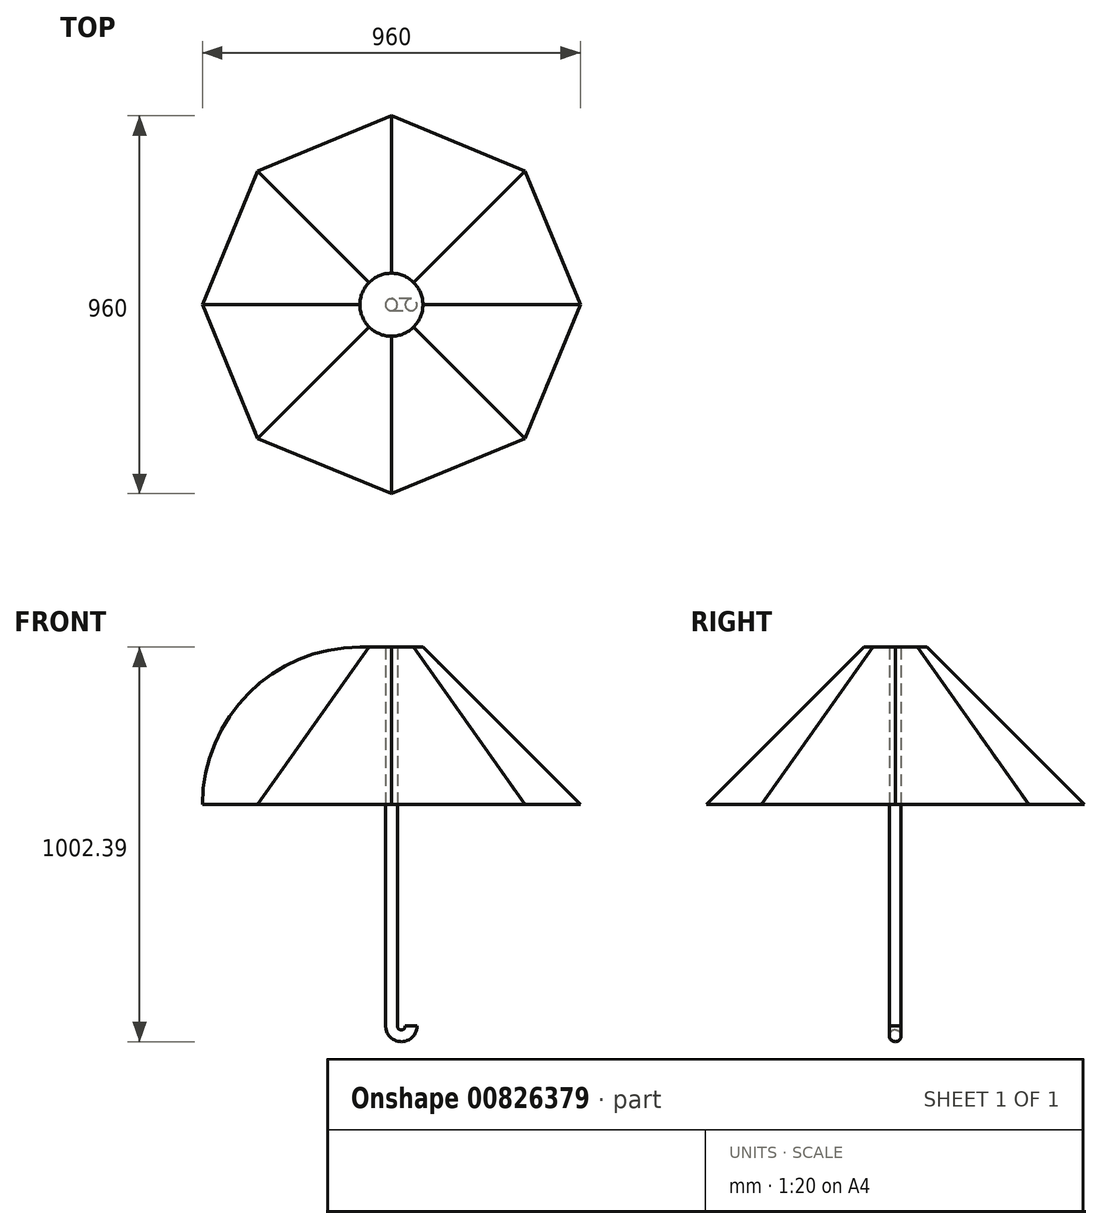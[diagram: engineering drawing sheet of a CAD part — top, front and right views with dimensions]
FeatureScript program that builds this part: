
annotation { "Feature Type Name" : "Feature", "Feature Type Description" : "" }
export const myFeature = defineFeature(function(context is Context, id is Id, definition is map)
    precondition{}
    {
        {
            var Q0;
            Q0=qCreatedBy(makeId("Top.planeOp"),FACE);
            cPlane(context, id + "F0", {"entities" : qUnion([Q0]), "cplaneType" : CPlaneType.OFFSET, "offset" : 400 * mm, "width" : 150 * mm, "height" : 150 * mm});
        }
        {
            var Q0;
            Q0=qCreatedBy(id+"F0.planeOp",FACE);
            var sketch = newSketch(context, id + "F1", { "sketchPlane" : qUnion([Q0])});
            skCircle(sketch, "E0", {"center": v(0, 0) * mm, "radius": 80 * mm});
            skSolve(sketch);
        }
        {
            var Q0;
            Q0=qCreatedBy(makeId("Top.planeOp"),FACE);
            var sketch = newSketch(context, id + "F2", { "sketchPlane" : qUnion([Q0])});
            skCircle(sketch, "E1.cCircle", {"center": v(0, 0) * mm, "radius": 443.46 * mm, "construction": true});
            skLineSegment(sketch, "E1.0", {"start": v(339.41, 339.41) * mm, "end": v(480, 0) * mm});
            skLineSegment(sketch, "E1.1", {"start": v(480, 0) * mm, "end": v(339.41, -339.41) * mm});
            skLineSegment(sketch, "E1.2", {"start": v(339.41, -339.41) * mm, "end": v(0, -480) * mm});
            skLineSegment(sketch, "E1.3", {"start": v(0, -480) * mm, "end": v(-339.41, -339.41) * mm});
            skLineSegment(sketch, "E1.4", {"start": v(-339.41, -339.41) * mm, "end": v(-480, 0) * mm});
            skLineSegment(sketch, "E1.5", {"start": v(-480, 0) * mm, "end": v(-339.41, 339.41) * mm});
            skLineSegment(sketch, "E1.6", {"start": v(-339.41, 339.41) * mm, "end": v(0, 480) * mm});
            skLineSegment(sketch, "E1.7", {"start": v(0, 480) * mm, "end": v(339.41, 339.41) * mm});
            skPoint(sketch, "E1.0.midPoint", {"position": v(409.7, 169.7) * mm});
            skSolve(sketch);
        }
        {
            var Q0;
            Q0=qCreatedBy(makeId("Front.planeOp"),FACE);
            var sketch = newSketch(context, id + "F3", { "sketchPlane" : qUnion([Q0])});
            skArc(sketch, "E2", {"start": v(-80, 400) * mm, "mid": v(-362.84, 282.84) * mm, "end": v(-480, 0) * mm});
            skSolve(sketch);
        }
        {
            var Q0;
            Q0=makeQuery(id+"F2.imprint","IMPRINT",FACE,{"disambiguationData":[TD([[makeQuery(id+"F2.imprint","IMPRINT",EDGE,{"derivedFrom":sQuery(id+"F2.wireOp",EDGE,"E1.0")}),-1.0]])]});
            var Q1;
            Q1=makeQuery(id+"F1.imprint","IMPRINT",FACE,{"disambiguationData":[TD([[makeQuery(id+"F1.imprint","IMPRINT",EDGE,{"derivedFrom":sQuery(id+"F1.wireOp",EDGE,"E0")}),1.0]])]});
            var Q2;
            Q2=sQuery(id+"F3.wireOp",EDGE,"E2");
            var Q3;
            Q3=sQuery(id+"Fi74ypTfE9Y1nCX_0.7.F3.wireOp",EDGE,"E2");
            var Q4;
            Q4=sQuery(id+"Fi74ypTfE9Y1nCX_0.1.F3.wireOp",EDGE,"E2");
            var Q5;
            Q5=sQuery(id+"Fi74ypTfE9Y1nCX_0.2.F3.wireOp",EDGE,"E2");
            var Q6;
            Q6=sQuery(id+"Fi74ypTfE9Y1nCX_0.3.F3.wireOp",EDGE,"E2");
            var Q7;
            Q7=sQuery(id+"Fi74ypTfE9Y1nCX_0.5.F3.wireOp",EDGE,"E2");
            var Q8;
            Q8=sQuery(id+"Fi74ypTfE9Y1nCX_0.6.F3.wireOp",EDGE,"E2");
            var Q9;
            Q9=sQuery(id+"Fi74ypTfE9Y1nCX_0.4.F3.wireOp",EDGE,"E2");
            var Q10;
            Q10=sQuery(id+"F1.wireOp",VERTEX,"E0.center");
            loft(context, id + "F4", {"addGuides" : true, "sheetProfilesArray" : [{ "sheetProfileEntities" : qUnion([Q0]) }, { "sheetProfileEntities" : qUnion([Q1]) }], "guidesArray" : [{ "guideEntities" : qUnion([Q2]), "guideDerivativeType" : LoftGuideDerivativeType.DEFAULT, "guideDerivativeMagnitude" : 1 }, { "guideEntities" : qUnion([Q3]), "guideDerivativeType" : LoftGuideDerivativeType.DEFAULT, "guideDerivativeMagnitude" : 1 }, { "guideEntities" : qUnion([Q4]), "guideDerivativeType" : LoftGuideDerivativeType.DEFAULT, "guideDerivativeMagnitude" : 1 }, { "guideEntities" : qUnion([Q5]), "guideDerivativeType" : LoftGuideDerivativeType.DEFAULT, "guideDerivativeMagnitude" : 1 }, { "guideEntities" : qUnion([Q6]), "guideDerivativeType" : LoftGuideDerivativeType.DEFAULT, "guideDerivativeMagnitude" : 1 }, { "guideEntities" : qUnion([Q7]), "guideDerivativeType" : LoftGuideDerivativeType.DEFAULT, "guideDerivativeMagnitude" : 1 }, { "guideEntities" : qUnion([Q8]), "guideDerivativeType" : LoftGuideDerivativeType.DEFAULT, "guideDerivativeMagnitude" : 1 }, { "guideEntities" : qUnion([Q9]), "guideDerivativeType" : LoftGuideDerivativeType.DEFAULT, "guideDerivativeMagnitude" : 1 }], "connections" : [{ "connectionEntities" : qUnion([Q10]), "connectionEdgeQueries" : qUnion([]), "connectionEdgeParameters" : [] }]});
        }
        {
            var Q0;
            Q0=makeQuery(id+"F4.opLoft","CAP_FACE",FACE,{"disambiguationData":[OSD([makeQuery(id+"F2.imprint","IMPRINT",FACE,{"disambiguationData":[TD([[makeQuery(id+"F2.imprint","IMPRINT",EDGE,{"derivedFrom":sQuery(id+"F2.wireOp",EDGE,"E1.0")}),-1.0]])]})])],"isStart":true});
            shell(context, id + "F5", {"entities" : qUnion([Q0]), "thickness" : 1 * mm});
        }
        {
            var Q0;
            Q0=qCreatedBy(makeId("Front.planeOp"),FACE);
            var sketch = newSketch(context, id + "F6", { "sketchPlane" : qUnion([Q0])});
            skLineSegment(sketch, "E3", {"start": v(0, 400) * mm, "end": v(0, -562.4) * mm});
            skArc(sketch, "E4", {"start": v(0, -562.4) * mm, "mid": v(25, -587.4) * mm, "end": v(50, -562.4) * mm});
            skSolve(sketch);
        }
        {
            var Q0;
            Q0=makeQuery(id+"F1.imprint","IMPRINT",FACE,{"disambiguationData":[TD([[makeQuery(id+"F1.imprint","IMPRINT",EDGE,{"derivedFrom":sQuery(id+"F1.wireOp",EDGE,"E0")}),1.0]])]});
            var sketch = newSketch(context, id + "F7", { "sketchPlane" : qUnion([Q0])});
            skCircle(sketch, "E5", {"center": v(0, 0) * mm, "radius": 15 * mm});
            skSolve(sketch);
        }
        {
            var Q0;
            Q0 = qSketchRegion(id + "F7", true);
            var Q1;
            Q1=sQuery(id+"F6.wireOp",EDGE,"E3");
            var Q2;
            Q2=sQuery(id+"F6.wireOp",EDGE,"E4");
            sweep(context, id + "F8", {"operationType" : NewBodyOperationType.ADD, "profiles" : qUnion([Q0]), "path" : qUnion([Q1, Q2])});
        }
    });
